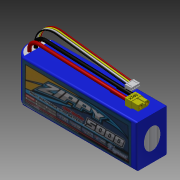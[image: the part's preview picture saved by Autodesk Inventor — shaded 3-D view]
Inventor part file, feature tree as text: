
AUTODESK INVENTOR PART (.ipt)
format: ipt  version: 2025 (Build 290162000, 162)  size: 1,127,936 bytes
history: native  units: mm
features: extrude x23, sketch x6, plane x4, pattern_linear x3, sweep x3, fillet x2, other x2, emboss x1, projected_geometry x1
ambient origin geometry x8: Origin, YZ Plane, XZ Plane, XY Plane, X Axis, Y Axis, Z Axis, Center Point
bodies: Solid1 (feature_tree)
feature tree (45):
  extrude  "Extrusion1"  Depth=51.0mm
  extrude  "Extrusion2"  Depth=2.0mm
  pattern_linear  "Rectangular Pattern1"  Spacing1=12.333333mm  [1 undecoded]
  fillet  "Fillet1"  Radius=105.0mm
  extrude  "Extrusion3"  Depth=2.0mm
  plane  "Work Plane1"
  extrude  "Extrusion4"  Depth=2.0mm
  extrude  "Extrusion5"  Depth=2.0mm
  extrude  "Extrusion6"  Depth=2.0mm TaperAngle=0.0deg
  extrude  "Extrusion7"  [1 undecoded]
  extrude  "Extrusion8"  Depth=2.0mm
  extrude  "Extrusion9"  Depth=2.0mm
  plane  "Work Plane2"
  emboss  "Emboss1"
  extrude  "Extrusion10"  Depth=2.0mm
  extrude  "Extrusion11"  Depth=2.0mm
  sketch  "3D Sketch1"
  sweep  "Sweep1"
  sweep  "Sweep2"
  extrude  "Extrusion12"  Depth=2.0mm TaperAngle=0.0deg
  plane  "Work Plane3"
  extrude  "Extrusion13"  Depth=2.0mm
  extrude  "Extrusion14"  Depth=2.0mm
  extrude  "Extrusion15"  Depth=2.0mm TaperAngle=0.0deg
  extrude  "Extrusion16"  Depth=2.0mm
  extrude  "Extrusion17"  Depth=2.0mm TaperAngle=0.0deg
  extrude  "Extrusion18"  Depth=2.0mm
  extrude  "Extrusion19"  Depth=2.0mm
  extrude  "Extrusion20"  Depth=2.0mm TaperAngle=0.0deg
  extrude  "Extrusion21"  Depth=10.0mm
  pattern_linear  "Rectangular Pattern2"  Spacing1=0.3mm  [1 undecoded]
  sweep  "Sweep3"
  pattern_linear  "Rectangular Pattern3"  Spacing1=4.93934mm  [1 undecoded]
  extrude  "Extrusion22"  Depth=2.0mm
  plane  "Work Plane4"
  extrude  "Extrusion23"  Depth=2.0mm
  fillet  "Fillet4"  Radius=10.0mm
  other  "Decal2"
  sketch  "Sketch Rectangular Pattern1"  dims[d0=37.0mm d1=51.0mm]
  sketch  "Sketch10"  dims[d5=2.0mm]
  sketch  "Sketch Rectangular Pattern2"  dims[d2=139.0mm d3=0.0mm d4=2.0mm]
  sketch  "3D Sketch2"
  projected_geometry  "Projected Loop1"
  sketch  "Sketch32"  dims[d6=37.0mm d7=12.333333mm d8=105.0mm d9=0.0mm d10=20.0mm d12=9.333333mm d13=2.0mm d14=8.0mm d15=105.0mm d16=0.0mm d17=-10.0mm d18=13.8mm d19=6.6mm d20=11.6mm d21=2.2mm d22=30.0mm d26=6.6mm d27=7.85mm d28=0.0mm d29=1.0mm d30=4.0mm d32=1.0mm d33=0.0mm d34=1.8mm d35=1.0mm d36=0.0mm d37=0.75mm d38=0.75mm d39=7.6mm d40=0.0mm d41=10.0mm d42=0.3mm d43=0.0mm d44=0.1mm d45=4.93934mm d46=0.70562mm d54=60.0mm d56=0.70562mm d57=10.0mm d59=10.0mm d61=0.3mm d62=0.0mm d63=1.0mm d64=0.0mm d65=4.3mm d67=3.4mm d68=0.3mm d69=0.0mm d70=3.5mm d71=3.5mm d72=4.0mm d73=4.0mm d74=0.3mm d75=0.0mm d76=3.9mm d77=3.9mm d78=7.8mm d80=10.0mm d81=13.5mm d82=13.5mm d83=10.0mm d84=10.0mm d85=0.0mm d86=0.0mm d87=10.337mm d88=20.0mm d89=0.0mm d90=-10.0mm d91=10.6mm d92=3.9mm d93=42.0mm d94=7.7mm d95=0.0mm d96=5.0mm d97=0.7mm d98=0.0mm d99=1.25mm d100=0.5mm d101=5.8mm d102=2.6mm d103=2.2mm d104=0.5mm d105=0.7mm d106=0.0mm d107=0.7mm d108=0.0mm d109=1.1mm d110=1.1mm d111=0.85mm d112=10.6mm d113=1.79mm d114=40.0mm d116=2.34mm d117=10.0mm d119=10.0mm d121=0.7mm d122=0.0mm d123=3.0mm d124=3.0mm d125=0.0mm d126=1.5mm d127=0.5mm d128=0.0mm d129=0.05mm d130=0.05mm d131=0.5mm d132=0.0mm d136=0.05mm d137=0.05mm d138=0.05mm d139=0.5mm d140=0.0mm d141=40.0mm d143=2.34mm d144=1.4mm d145=1.4mm d146=10.253mm d147=5.0mm d148=28.0mm d149=25.0mm d150=0.0mm d151=40.0mm d153=2.34mm d154=0.2mm d155=0.5mm d156=0.0mm d157=0.1mm d158=10.0mm d159=13.0mm d160=0.1mm d161=0.0mm d166=2.0mm d174=0.0mm d175=0.0mm d176=0.0mm]
  other  "Image2"
note: 4 required parameter values undecoded (feature->parameter linkage not recoverable at this tier; creation-order binding heuristic only, values carry confidence <= 0.55)
